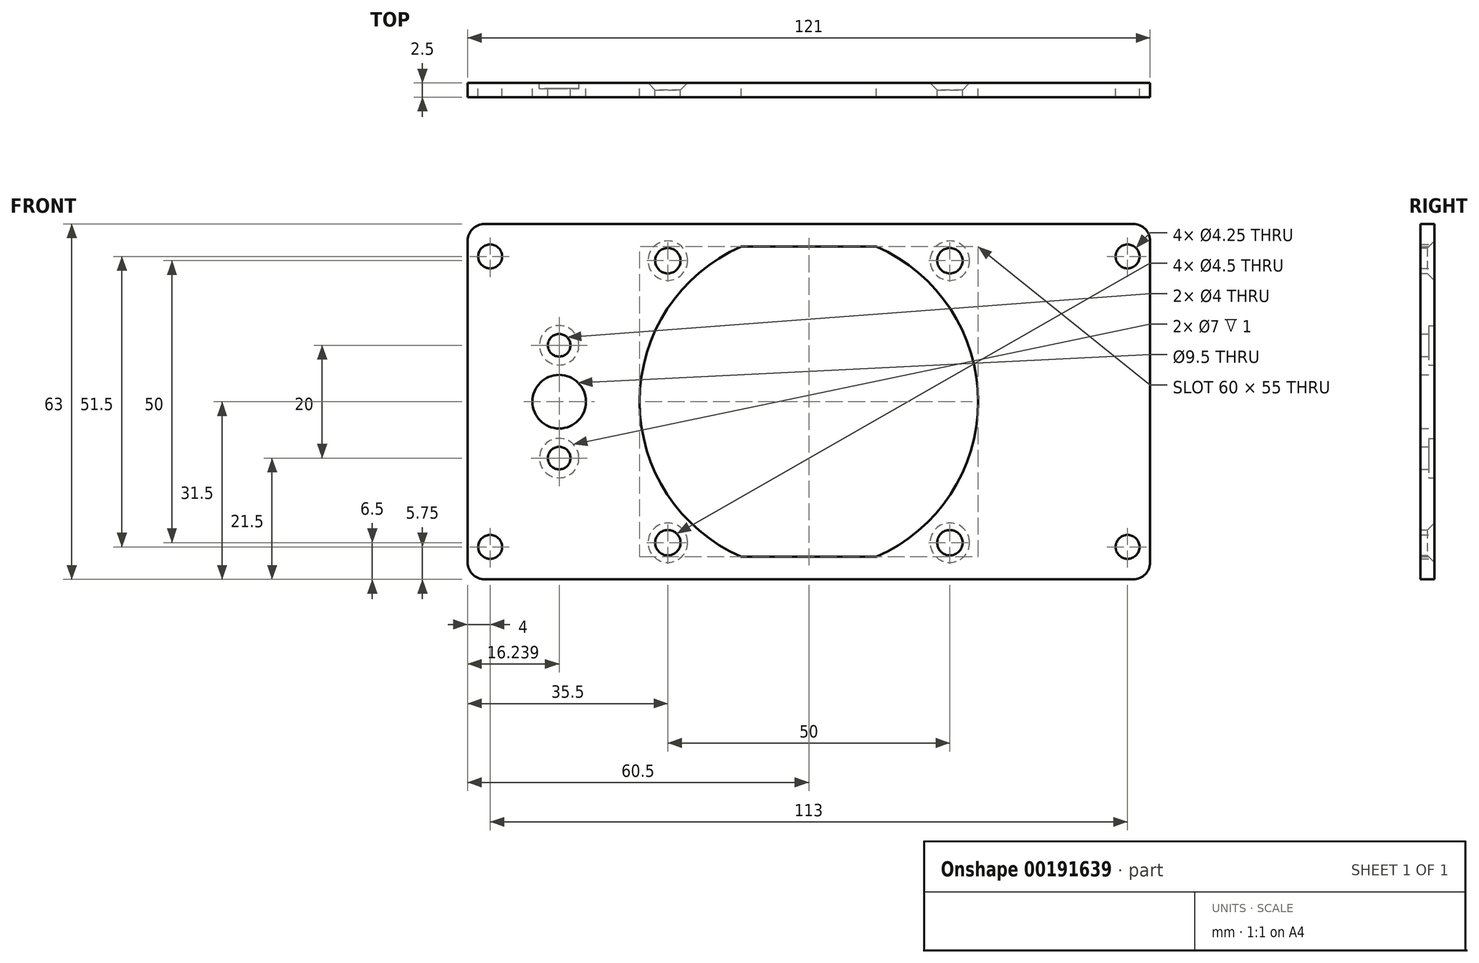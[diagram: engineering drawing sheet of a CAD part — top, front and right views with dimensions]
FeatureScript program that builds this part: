
annotation { "Feature Type Name" : "Feature", "Feature Type Description" : "" }
export const myFeature = defineFeature(function(context is Context, id is Id, definition is map)
    precondition{}
    {
        {
            var Q0;
            Q0=qCreatedBy(makeId("Front.planeOp"),FACE);
            var sketch = newSketch(context, id + "F0", { "sketchPlane" : qUnion([Q0])});
            skLineSegment(sketch, "E0.bottom", {"start": v(57.5, 31.5) * mm, "end": v(-57.5, 31.5) * mm});
            skLineSegment(sketch, "E0.top", {"start": v(57.5, -31.5) * mm, "end": v(-57.5, -31.5) * mm});
            skLineSegment(sketch, "E0.left", {"start": v(60.5, 28.5) * mm, "end": v(60.5, -28.5) * mm});
            skLineSegment(sketch, "E0.right", {"start": v(-60.5, 28.5) * mm, "end": v(-60.5, -28.5) * mm});
            skPoint(sketch, "E0.middle", {"position": v(0, 0) * mm});
            skLineSegment(sketch, "E1.bottom", {"start": v(56.5, 25.75) * mm, "end": v(-56.5, 25.75) * mm, "construction": true});
            skLineSegment(sketch, "E1.top", {"start": v(56.5, -25.75) * mm, "end": v(-56.5, -25.75) * mm, "construction": true});
            skLineSegment(sketch, "E1.left", {"start": v(56.5, 25.75) * mm, "end": v(56.5, -25.75) * mm, "construction": true});
            skLineSegment(sketch, "E1.right", {"start": v(-56.5, 25.75) * mm, "end": v(-56.5, -25.75) * mm, "construction": true});
            skCircle(sketch, "E2", {"center": v(0, 0) * mm, "radius": 30 * mm});
            skLineSegment(sketch, "E3.bottom", {"start": v(25, 25) * mm, "end": v(-25, 25) * mm, "construction": true});
            skLineSegment(sketch, "E3.top", {"start": v(25, -25) * mm, "end": v(-25, -25) * mm, "construction": true});
            skLineSegment(sketch, "E3.left", {"start": v(25, 25) * mm, "end": v(25, -25) * mm, "construction": true});
            skLineSegment(sketch, "E3.right", {"start": v(-25, 25) * mm, "end": v(-25, -25) * mm, "construction": true});
            skPoint(sketch, "E4.visualSharp", {"position": v(60.5, 31.5) * mm});
            skArc(sketch, "E4.filletArc", {"start": v(60.5, 28.5) * mm, "mid": v(59.62, 30.62) * mm, "end": v(57.5, 31.5) * mm});
            skPoint(sketch, "E5.visualSharp", {"position": v(60.5, -31.5) * mm});
            skArc(sketch, "E5.filletArc", {"start": v(57.5, -31.5) * mm, "mid": v(59.62, -30.62) * mm, "end": v(60.5, -28.5) * mm});
            skPoint(sketch, "E6.visualSharp", {"position": v(-60.5, -31.5) * mm});
            skArc(sketch, "E6.filletArc", {"start": v(-60.5, -28.5) * mm, "mid": v(-59.62, -30.62) * mm, "end": v(-57.5, -31.5) * mm});
            skPoint(sketch, "E7.visualSharp", {"position": v(-60.5, 31.5) * mm});
            skArc(sketch, "E7.filletArc", {"start": v(-57.5, 31.5) * mm, "mid": v(-59.62, 30.62) * mm, "end": v(-60.5, 28.5) * mm});
            skLineSegment(sketch, "E8", {"start": v(-44.26, 25.75) * mm, "end": v(-44.26, -25.75) * mm, "construction": true});
            skCircle(sketch, "E9", {"center": v(-44.26, 0) * mm, "radius": 4.75 * mm});
            skPoint(sketch, "E10", {"position": v(-44.26, 10) * mm});
            skPoint(sketch, "E11", {"position": v(-44.26, -10) * mm});
            skLineSegment(sketch, "E12", {"start": v(11.99, 27.5) * mm, "end": v(-11.99, 27.5) * mm});
            skLineSegment(sketch, "E13", {"start": v(11.99, -27.5) * mm, "end": v(-11.99, -27.5) * mm});
            skSolve(sketch);
        }
        {
            var Q0;
            Q0=makeQuery(id+"F0.imprint","IMPRINT",FACE,{"disambiguationData":[TD([[makeQuery(id+"F0.imprint","IMPRINT",EDGE,{"derivedFrom":sQuery(id+"F0.wireOp",EDGE,"E0.bottom")}),1.0]])]});
            var Q1;
            {var subQ0=sQuery(id+"F0.wireOp",EDGE,"E12");Q1=makeQuery(id+"F0.imprint","IMPRINT",FACE,{"disambiguationData":[TD([[makeQuery(id+"F0.imprint","IMPRINT",EDGE,{"derivedFrom":subQ0}),-1.0]])]});}
            var Q2;
            {var subQ0=sQuery(id+"F0.wireOp",EDGE,"E13");Q2=makeQuery(id+"F0.imprint","IMPRINT",FACE,{"disambiguationData":[TD([[makeQuery(id+"F0.imprint","IMPRINT",EDGE,{"derivedFrom":subQ0}),1.0]])]});}
            extrude(context, id + "F1", {"entities" : qUnion([Q0, Q1, Q2]), "depth" : 2.5 * mm});
        }
        {
            var Q0;
            Q0=sQuery(id+"F0.wireOp",VERTEX,"E1.bottom.end");
            var Q1;
            Q1=sQuery(id+"F0.wireOp",VERTEX,"E1.left.start");
            var Q2;
            Q2=sQuery(id+"F0.wireOp",VERTEX,"E1.top.start");
            var Q3;
            Q3=sQuery(id+"F0.wireOp",VERTEX,"E1.top.end");
            var Q4;
            Q4=makeQuery(id+"F1.opExtrude","SWEPT_BODY",BODY,{"disambiguationData":[OSD([sQuery(id+"F0.wireOp",EDGE,"E0.bottom"),sQuery(id+"F0.wireOp",EDGE,"E0.top"),sQuery(id+"F0.wireOp",EDGE,"E0.left"),sQuery(id+"F0.wireOp",EDGE,"E0.right"),sQuery(id+"F0.wireOp",EDGE,"E2"),sQuery(id+"F0.wireOp",EDGE,"E4.filletArc"),sQuery(id+"F0.wireOp",EDGE,"E5.filletArc"),sQuery(id+"F0.wireOp",EDGE,"E6.filletArc"),sQuery(id+"F0.wireOp",EDGE,"E7.filletArc")])]});
            hole(context, id + "F2", {"style" : HoleStyle.SIMPLE, "endStyle" : HoleEndStyle.THROUGH, "oppositeDirection" : true, "holeDiameter" : 4.25 * mm, "locations" : qUnion([Q0, Q1, Q2, Q3]), "scope" : qUnion([Q4]), "isTappedThrough" : true});
        }
        {
            var Q0;
            Q0=sQuery(id+"F0.wireOp",VERTEX,"E3.right.start");
            var Q1;
            Q1=sQuery(id+"F0.wireOp",VERTEX,"E3.bottom.start");
            var Q2;
            Q2=sQuery(id+"F0.wireOp",VERTEX,"E3.top.start");
            var Q3;
            Q3=sQuery(id+"F0.wireOp",VERTEX,"E3.right.end");
            var Q4;
            Q4=makeQuery(id+"F1.opExtrude","SWEPT_BODY",BODY,{"disambiguationData":[OSD([sQuery(id+"F0.wireOp",EDGE,"E0.bottom"),sQuery(id+"F0.wireOp",EDGE,"E0.top"),sQuery(id+"F0.wireOp",EDGE,"E0.left"),sQuery(id+"F0.wireOp",EDGE,"E0.right"),sQuery(id+"F0.wireOp",EDGE,"E2"),sQuery(id+"F0.wireOp",EDGE,"E4.filletArc"),sQuery(id+"F0.wireOp",EDGE,"E5.filletArc"),sQuery(id+"F0.wireOp",EDGE,"E6.filletArc"),sQuery(id+"F0.wireOp",EDGE,"E7.filletArc")])]});
            hole(context, id + "F3", {"style" : HoleStyle.C_SINK, "endStyle" : HoleEndStyle.THROUGH, "oppositeDirection" : true, "holeDiameter" : 4.5 * mm, "cSinkDiameter" : 7 * mm, "cSinkAngle" : 90 * degree, "locations" : qUnion([Q0, Q1, Q2, Q3]), "scope" : qUnion([Q4]), "isTappedThrough" : true});
        }
        {
            var Q0;
            Q0=sQuery(id+"F0.wireOp",VERTEX,"E10");
            var Q1;
            Q1=sQuery(id+"F0.wireOp",VERTEX,"E11");
            var Q2;
            Q2=makeQuery(id+"F1.opExtrude","SWEPT_BODY",BODY,{"disambiguationData":[OSD([sQuery(id+"F0.wireOp",EDGE,"E0.bottom"),sQuery(id+"F0.wireOp",EDGE,"E0.top"),sQuery(id+"F0.wireOp",EDGE,"E0.left"),sQuery(id+"F0.wireOp",EDGE,"E0.right"),sQuery(id+"F0.wireOp",EDGE,"E2"),sQuery(id+"F0.wireOp",EDGE,"E4.filletArc"),sQuery(id+"F0.wireOp",EDGE,"E5.filletArc"),sQuery(id+"F0.wireOp",EDGE,"E6.filletArc"),sQuery(id+"F0.wireOp",EDGE,"E7.filletArc"),sQuery(id+"F0.wireOp",EDGE,"E9")])]});
            hole(context, id + "F4", {"style" : HoleStyle.C_BORE, "endStyle" : HoleEndStyle.THROUGH, "oppositeDirection" : true, "holeDiameter" : 4 * mm, "cBoreDiameter" : 7 * mm, "cBoreDepth" : 1 * mm, "locations" : qUnion([Q0, Q1]), "scope" : qUnion([Q2]), "isTappedThrough" : true});
        }
    });
